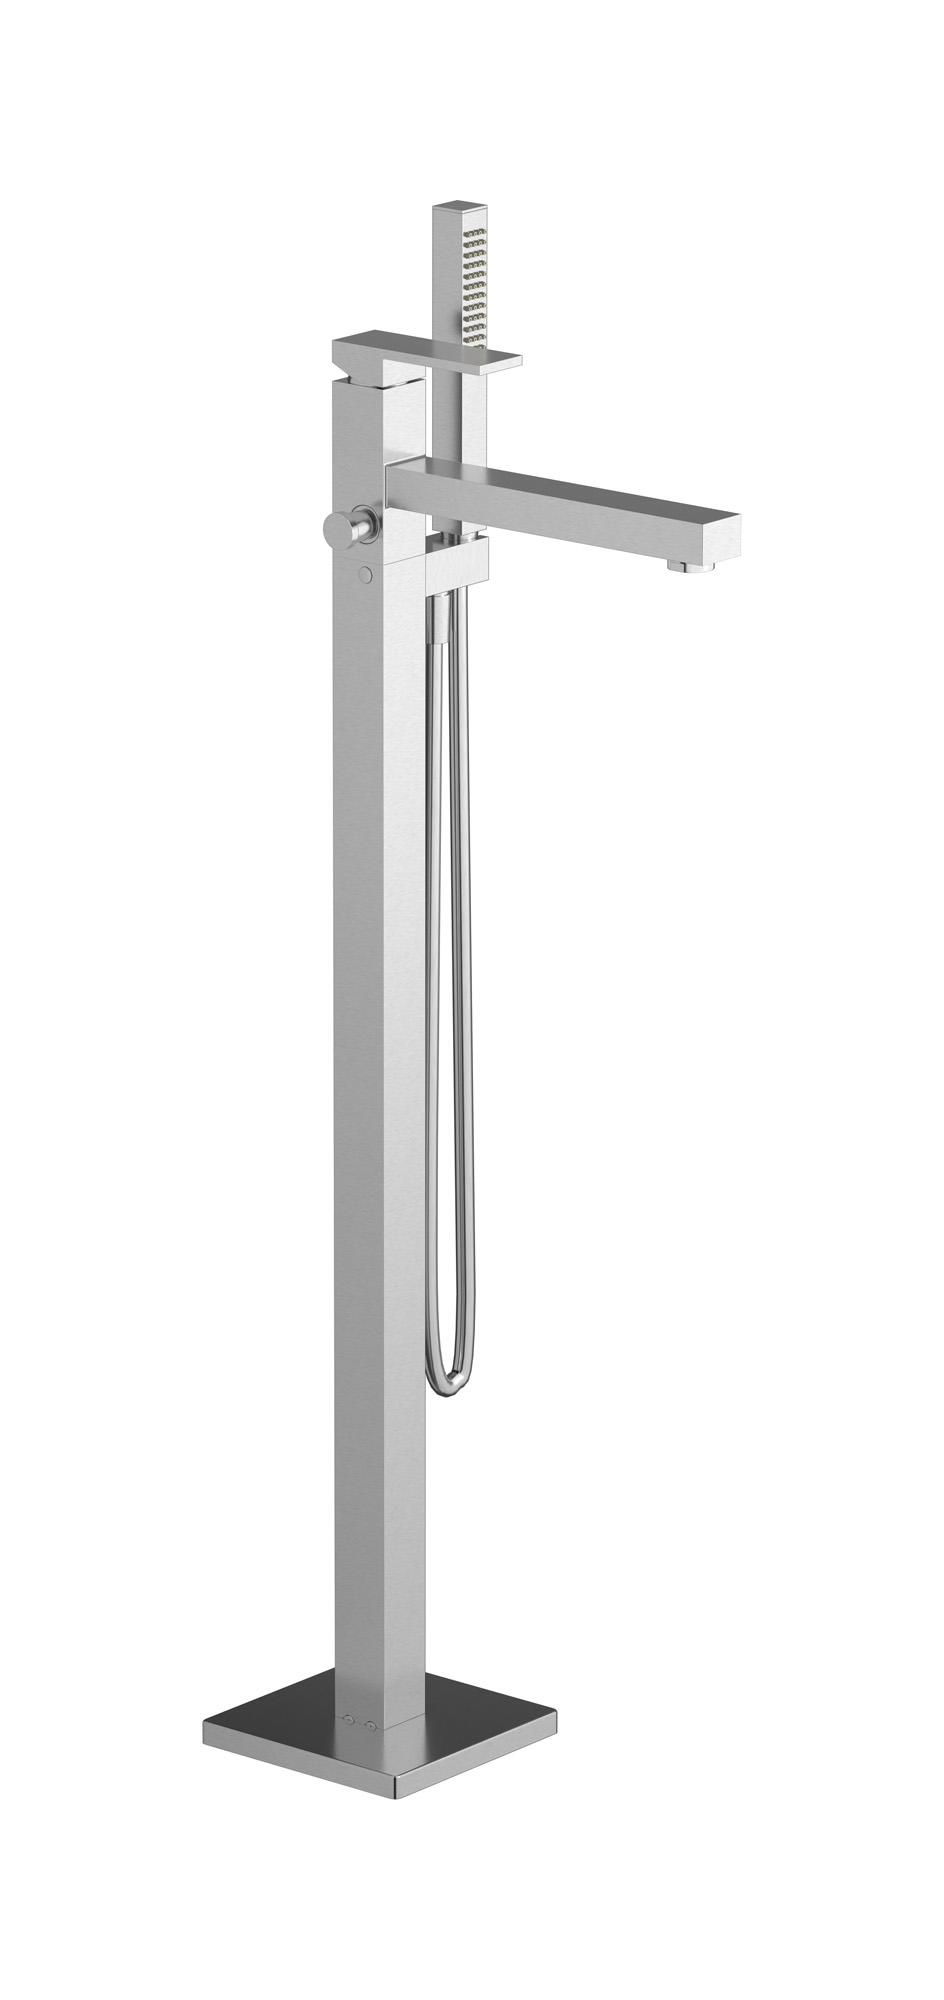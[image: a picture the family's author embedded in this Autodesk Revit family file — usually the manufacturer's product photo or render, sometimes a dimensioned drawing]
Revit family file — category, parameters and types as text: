
# Revit family: RU399
name_source: partatom
category: Apparecchi idraulici
units: mm (PartAtom-declared; Revit-internal decimal feet)

## family parameters
Basato su piano di lavoro = No
Condiviso = No
Mantieni orientamento annotazione = No
Numero OmniClass = 23.45.55.17
Punto di calcolo locali = No
Quota connettore circolare = Usa diametro
Sempre verticale = Sì
Taglio con vuoti quando caricato = No
Tipo di parte = Normale
Titolo OmniClass = Mixing Faucets

## types (12) — shared parameters
Cold water inlet = 10 mm  [stored 0.0328084 ft]
Commenti sul tipo = Freestanding bath filler
Connessione CW = No
Connessione HW = No
Connessione di scarico = No
Connessione di ventilazione = No
Descrizione = Freestanding bath filler
Hot water inlet = 10 mm  [stored 0.0328084 ft]
Produttore = IB Rubinetterie S.p.A.
URL = https://www.weareib.it
zero-valued in all types: Prospetto di default

## per-type parameters (varying)
| type | Finishes surface | Immagine tipo | Modello |
| Chrome | IB_Chrome | RU399CC.jpg | RU399CC |
| Matt White | IB_matt white | RU399BO.jpg | RU399BO |
| Black Chrome | IB_Black chrome | RU399CF.jpg | RU399CF |
| Brushed Black Chrome | IB_Brushed black chrome | RU399CS.jpg | RU399CS |
| Pale Gold | IB_Pale gold | RU399II.jpg | RU399II |
| Brushed Pale Gold | IB_brushed pale gold | RU399IS.jpg | RU399IS |
| Matt Black | IB_matt black | RU399NP.jpg | RU399NP |
| Gold | IB_gold | RU399OO.jpg | RU399OO |
| Brushed Gold | IB_brushed gold | RU399OS.jpg | RU399OS |
| Rose Gold | IB_Rose gold | RU399RS.jpg | RU399RS |
| Brushed Rose Gold | IB_Brushed rose gold | RU399SR.jpg | RU399SR |
| Brushed Nickel | IB_Brushed nickel | RU399SS.jpg | RU399SS |

note: [stored X ft] marks values corroborated as IEEE doubles in the binary element streams (Revit-internal decimal feet)
